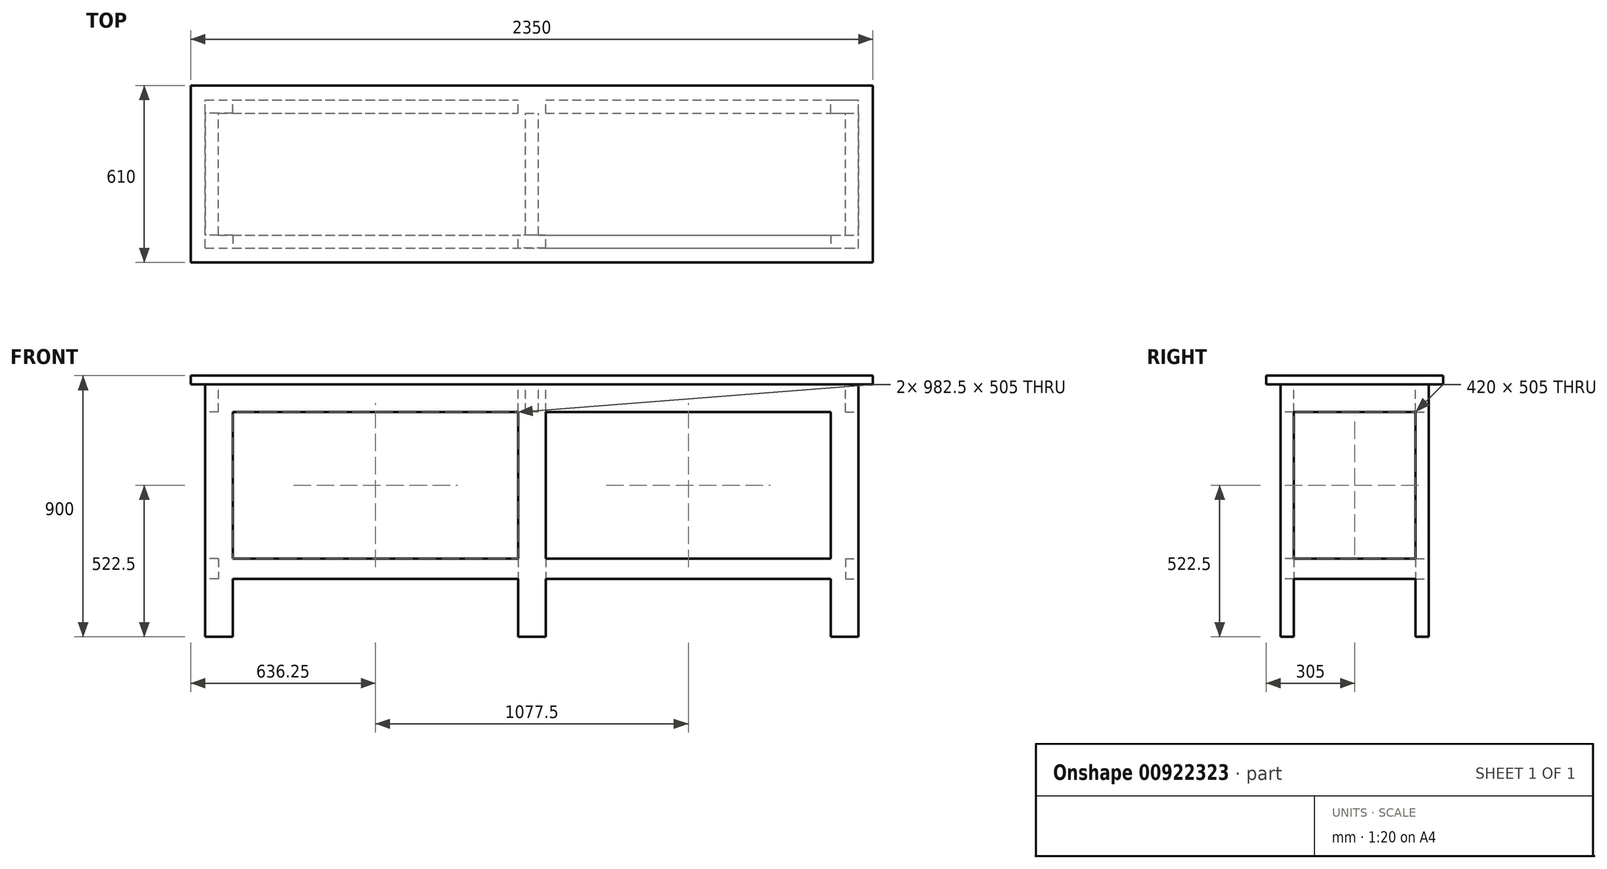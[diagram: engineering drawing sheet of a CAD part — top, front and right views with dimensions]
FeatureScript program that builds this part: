
annotation { "Feature Type Name" : "Feature", "Feature Type Description" : "" }
export const myFeature = defineFeature(function(context is Context, id is Id, definition is map)
    precondition{}
    {
        {
            var Q0;
            Q0=qCreatedBy(makeId("Top.planeOp"),FACE);
            cPlane(context, id + "F0", {"entities" : qUnion([Q0]), "cplaneType" : CPlaneType.OFFSET, "offset" : 900 * mm, "width" : 150 * mm, "height" : 150 * mm});
        }
        {
            var Q0;
            Q0=qCreatedBy(id+"F0.planeOp",FACE);
            var sketch = newSketch(context, id + "F1", { "sketchPlane" : qUnion([Q0])});
            skLineSegment(sketch, "E0.bottom", {"start": v(1175, -305) * mm, "end": v(-1175, -305) * mm});
            skLineSegment(sketch, "E0.top", {"start": v(1175, 305) * mm, "end": v(-1175, 305) * mm});
            skLineSegment(sketch, "E0.left", {"start": v(1175, -305) * mm, "end": v(1175, 305) * mm});
            skLineSegment(sketch, "E0.right", {"start": v(-1175, -305) * mm, "end": v(-1175, 305) * mm});
            skPoint(sketch, "E0.middle", {"position": v(0, 0) * mm});
            skSolve(sketch);
        }
        {
            var Q0;
            Q0=makeQuery(id+"F1.imprint","IMPRINT",FACE,{"disambiguationData":[TD([[makeQuery(id+"F1.imprint","IMPRINT",EDGE,{"derivedFrom":sQuery(id+"F1.wireOp",EDGE,"E0.bottom")}),-1.0]])]});
            extrude(context, id + "F2", {"entities" : qUnion([Q0]), "oppositeDirection" : true, "depth" : 30 * mm, "offsetDistance" : 25 * mm});
        }
        {
            var Q0;
            Q0=makeQuery(id+"F2.opExtrude","CAP_FACE",FACE,{"disambiguationData":[OSD([sQuery(id+"F1.wireOp",EDGE,"E0.bottom"),sQuery(id+"F1.wireOp",EDGE,"E0.top"),sQuery(id+"F1.wireOp",EDGE,"E0.left"),sQuery(id+"F1.wireOp",EDGE,"E0.right")])],"isStart":false});
            var sketch = newSketch(context, id + "F3", { "sketchPlane" : qUnion([Q0])});
            skLineSegment(sketch, "E1.bottom", {"start": v(-1125, 255) * mm, "end": v(-1030, 255) * mm});
            skLineSegment(sketch, "E1.top", {"start": v(-1125, -255) * mm, "end": v(1125, -255) * mm});
            skLineSegment(sketch, "E1.left", {"start": v(-1125, 255) * mm, "end": v(-1125, -255) * mm});
            skLineSegment(sketch, "E1.right", {"start": v(1125, 255) * mm, "end": v(1125, -255) * mm});
            skPoint(sketch, "E1.middle", {"position": v(0, 0) * mm});
            skLineSegment(sketch, "E2.bottom", {"start": v(-1080, 210) * mm, "end": v(-47.5, 210) * mm});
            skLineSegment(sketch, "E2.top", {"start": v(-1080, -210) * mm, "end": v(1080, -210) * mm});
            skLineSegment(sketch, "E2.left", {"start": v(-1080, 210) * mm, "end": v(-1080, -210) * mm});
            skLineSegment(sketch, "E2.right", {"start": v(1080, 210) * mm, "end": v(1080, -210) * mm});
            skLineSegment(sketch, "E3", {"start": v(-1080, 210) * mm, "end": v(-1125, 210) * mm});
            skPoint(sketch, "E4", {"position": v(-1030, 210) * mm});
            skLineSegment(sketch, "E5", {"start": v(-1030, 210) * mm, "end": v(-1030, 255) * mm});
            skLineSegment(sketch, "E6", {"start": v(0, 0) * mm, "end": v(0, 95) * mm, "construction": true});
            skLineSegment(sketch, "E7", {"start": v(0, 0) * mm, "end": v(-86.34, 0) * mm, "construction": true});
            skLineSegment(sketch, "E8.MirrorCS", {"start": v(-1080, -210) * mm, "end": v(-1125, -210) * mm});
            skLineSegment(sketch, "E9.MirrorCS", {"start": v(-1030, -210) * mm, "end": v(-1030, -255) * mm});
            skLineSegment(sketch, "E10.MirrorCS", {"start": v(1030, 210) * mm, "end": v(1030, 255) * mm});
            skLineSegment(sketch, "E11.MirrorCS", {"start": v(1080, 210) * mm, "end": v(1125, 210) * mm});
            skLineSegment(sketch, "E12.MirrorCS", {"start": v(1030, -210) * mm, "end": v(1030, -255) * mm});
            skLineSegment(sketch, "E13.MirrorCS", {"start": v(1080, -210) * mm, "end": v(1125, -210) * mm});
            skLineSegment(sketch, "E14.bottom", {"start": v(22.5, 210) * mm, "end": v(-22.5, 210) * mm});
            skLineSegment(sketch, "E14.top", {"start": v(22.5, -210) * mm, "end": v(-22.5, -210) * mm});
            skLineSegment(sketch, "E14.left", {"start": v(22.5, 210) * mm, "end": v(22.5, -210) * mm});
            skLineSegment(sketch, "E14.right", {"start": v(-22.5, 210) * mm, "end": v(-22.5, -210) * mm});
            skPoint(sketch, "E15.oppositeSnap0", {"position": v(0, 47.5) * mm});
            skLineSegment(sketch, "E15.left", {"start": v(22.5, -47.5) * mm, "end": v(22.5, 47.5) * mm});
            skLineSegment(sketch, "E16", {"start": v(0, -210) * mm, "end": v(0, -255) * mm, "construction": true});
            skLineSegment(sketch, "E17", {"start": v(0, 210) * mm, "end": v(0, 255) * mm, "construction": true});
            skLineSegment(sketch, "E18.bottom", {"start": v(47.5, 255) * mm, "end": v(-47.5, 255) * mm});
            skLineSegment(sketch, "E18.top", {"start": v(47.5, 210) * mm, "end": v(-47.5, 210) * mm});
            skLineSegment(sketch, "E18.left", {"start": v(47.5, 255) * mm, "end": v(47.5, 210) * mm});
            skLineSegment(sketch, "E18.right", {"start": v(-47.5, 255) * mm, "end": v(-47.5, 210) * mm});
            skPoint(sketch, "E18.middle", {"position": v(0, 232.5) * mm});
            skLineSegment(sketch, "E19.bottom", {"start": v(47.5, -210) * mm, "end": v(-47.5, -210) * mm});
            skLineSegment(sketch, "E19.top", {"start": v(47.5, -255) * mm, "end": v(-47.5, -255) * mm});
            skLineSegment(sketch, "E19.left", {"start": v(47.5, -210) * mm, "end": v(47.5, -255) * mm});
            skLineSegment(sketch, "E19.right", {"start": v(-47.5, -210) * mm, "end": v(-47.5, -255) * mm});
            skPoint(sketch, "E19.middle", {"position": v(0, -232.5) * mm});
            skLineSegment(sketch, "E20", {"start": v(-1030, 255) * mm, "end": v(-47.5, 255) * mm});
            skLineSegment(sketch, "E21", {"start": v(-47.5, 255) * mm, "end": v(47.5, 255) * mm});
            skLineSegment(sketch, "E22", {"start": v(47.5, 255) * mm, "end": v(1125, 255) * mm});
            skLineSegment(sketch, "E23", {"start": v(47.5, 210) * mm, "end": v(1080, 210) * mm});
            skLineSegment(sketch, "E24", {"start": v(-47.5, 210) * mm, "end": v(47.5, 210) * mm});
            skSolve(sketch);
        }
        {
            var Q0;
            Q0=makeQuery(id+"F3.imprint","IMPRINT",FACE,{"disambiguationData":[TD([[makeQuery(id+"F3.imprint","IMPRINT",EDGE,{"derivedFrom":sQuery(id+"F3.wireOp",EDGE,"E2.left")}),-1.0]])]});
            var Q1;
            Q1=makeQuery(id+"F3.imprint","IMPRINT",FACE,{"disambiguationData":[TD([[makeQuery(id+"F3.imprint","IMPRINT",EDGE,{"derivedFrom":sQuery(id+"F3.wireOp",EDGE,"E2.right")}),1.0]])]});
            var Q2;
            {var subQ3=sQuery(id+"F3.wireOp",EDGE,"E5");Q2=makeQuery(id+"F3.imprint","IMPRINT",FACE,{"disambiguationData":[TD([[makeQuery(id+"F3.imprint","IMPRINT",EDGE,{"derivedFrom":subQ3}),-1.0]])]});}
            var Q3;
            {var subQ0=sQuery(id+"F3.wireOp",EDGE,"E9.MirrorCS");Q3=makeQuery(id+"F3.imprint","IMPRINT",FACE,{"disambiguationData":[TD([[makeQuery(id+"F3.imprint","IMPRINT",EDGE,{"derivedFrom":subQ0}),1.0]])]});}
            var Q4;
            {var subQ3=sQuery(id+"F3.wireOp",EDGE,"E14.bottom");Q4=makeQuery(id+"F3.imprint","IMPRINT",FACE,{"disambiguationData":[TD([[makeQuery(id+"F3.imprint","IMPRINT",EDGE,{"derivedFrom":subQ3}),1.0]])]});}
            var Q5;
            {var subQ0=sQuery(id+"F3.wireOp",EDGE,"E10.MirrorCS");Q5=makeQuery(id+"F3.imprint","IMPRINT",FACE,{"disambiguationData":[TD([[makeQuery(id+"F3.imprint","IMPRINT",EDGE,{"derivedFrom":subQ0}),1.0]])]});}
            var Q6;
            {var subQ1=sQuery(id+"F3.wireOp",EDGE,"E14.right");Q6=makeQuery(id+"F3.imprint","IMPRINT",FACE,{"disambiguationData":[TD([[makeQuery(id+"F3.imprint","IMPRINT",EDGE,{"derivedFrom":subQ1}),1.0]])]});}
            var Q7;
            {var subQ0=sQuery(id+"F3.wireOp",EDGE,"E12.MirrorCS");Q7=makeQuery(id+"F3.imprint","IMPRINT",FACE,{"disambiguationData":[TD([[makeQuery(id+"F3.imprint","IMPRINT",EDGE,{"derivedFrom":subQ0}),-1.0]])]});}
            extrude(context, id + "F4", {"entities" : qUnion([Q0, Q1, Q2, Q3, Q4, Q5, Q6, Q7]), "operationType" : NewBodyOperationType.ADD, "depth" : 95 * mm, "offsetDistance" : 25 * mm});
        }
        {
            var Q0;
            {var subQ0=sQuery(id+"F3.wireOp",EDGE,"E3");Q0=makeQuery(id+"F3.imprint","IMPRINT",FACE,{"disambiguationData":[TD([[makeQuery(id+"F3.imprint","IMPRINT",EDGE,{"derivedFrom":subQ0}),-1.0]])]});}
            var Q1;
            {var subQ0=sQuery(id+"F3.wireOp",EDGE,"E8.MirrorCS");Q1=makeQuery(id+"F3.imprint","IMPRINT",FACE,{"disambiguationData":[TD([[makeQuery(id+"F3.imprint","IMPRINT",EDGE,{"derivedFrom":subQ0}),1.0]])]});}
            var Q2;
            {var subQ0=sQuery(id+"F3.wireOp",EDGE,"E12.MirrorCS");Q2=makeQuery(id+"F3.imprint","IMPRINT",FACE,{"disambiguationData":[TD([[makeQuery(id+"F3.imprint","IMPRINT",EDGE,{"derivedFrom":subQ0}),1.0]])]});}
            var Q3;
            {var subQ0=sQuery(id+"F3.wireOp",EDGE,"E10.MirrorCS");Q3=makeQuery(id+"F3.imprint","IMPRINT",FACE,{"disambiguationData":[TD([[makeQuery(id+"F3.imprint","IMPRINT",EDGE,{"derivedFrom":subQ0}),-1.0]])]});}
            var Q4;
            Q4=makeQuery(id+"F3.imprint","IMPRINT",FACE,{"disambiguationData":[TD([[makeQuery(id+"F3.imprint","IMPRINT",EDGE,{"derivedFrom":sQuery(id+"F3.wireOp",EDGE,"E15.bottom")}),1.0]])]});
            var Q5;
            Q5=makeQuery(id+"F3.imprint","IMPRINT",FACE,{"disambiguationData":[TD([[makeQuery(id+"F3.imprint","IMPRINT",EDGE,{"derivedFrom":sQuery(id+"F3.wireOp",EDGE,"E18.bottom")}),1.0]])]});
            var Q6;
            Q6=makeQuery(id+"F3.imprint","IMPRINT",FACE,{"disambiguationData":[TD([[makeQuery(id+"F3.imprint","IMPRINT",EDGE,{"derivedFrom":sQuery(id+"F3.wireOp",EDGE,"E19.top")}),-1.0]])]});
            var Q7;
            {var subQ3=sQuery(id+"F3.wireOp",EDGE,"E18.left");Q7=makeQuery(id+"F3.imprint","IMPRINT",FACE,{"disambiguationData":[TD([[makeQuery(id+"F3.imprint","IMPRINT",EDGE,{"derivedFrom":subQ3}),-1.0]])]});}
            extrude(context, id + "F5", {"entities" : qUnion([Q0, Q1, Q2, Q3, Q4, Q5, Q6, Q7]), "operationType" : NewBodyOperationType.ADD, "depth" : (900 - 30) * mm, "offsetDistance" : 25 * mm});
        }
        {
            var Q0;
            Q0=qCreatedBy(makeId("Top.planeOp"),FACE);
            cPlane(context, id + "F6", {"entities" : qUnion([Q0]), "cplaneType" : CPlaneType.OFFSET, "offset" : 200 * mm, "width" : 150 * mm, "height" : 150 * mm});
        }
        {
            var Q0;
            Q0=qCreatedBy(id+"F6.planeOp",FACE);
            var sketch = newSketch(context, id + "F7", { "sketchPlane" : qUnion([Q0])});
            skLineSegment(sketch, "E25.bottom", {"start": v(-1030, 255) * mm, "end": v(1030, 255) * mm});
            skLineSegment(sketch, "E25.top", {"start": v(-1030, -255) * mm, "end": v(1030, -255) * mm});
            skLineSegment(sketch, "E25.left", {"start": v(-1125, 210) * mm, "end": v(-1125, -210) * mm});
            skLineSegment(sketch, "E25.right", {"start": v(1125, 210) * mm, "end": v(1125, -210) * mm});
            skPoint(sketch, "E25.middle", {"position": v(0, 0) * mm});
            skLineSegment(sketch, "E26.bottom", {"start": v(-1030, 210) * mm, "end": v(1030, 210) * mm});
            skLineSegment(sketch, "E26.top", {"start": v(-1030, -210) * mm, "end": v(1030, -210) * mm});
            skLineSegment(sketch, "E26.left", {"start": v(-1080, 210) * mm, "end": v(-1080, -210) * mm});
            skLineSegment(sketch, "E26.right", {"start": v(1080, 210) * mm, "end": v(1080, -210) * mm});
            skLineSegment(sketch, "E27", {"start": v(-1080, 210) * mm, "end": v(-1125, 210) * mm});
            skPoint(sketch, "E28", {"position": v(-1030, 210) * mm});
            skLineSegment(sketch, "E29", {"start": v(-1030, 210) * mm, "end": v(-1030, 255) * mm});
            skLineSegment(sketch, "E30.MirrorCS", {"start": v(-1080, -210) * mm, "end": v(-1125, -210) * mm});
            skLineSegment(sketch, "E31.MirrorCS", {"start": v(-1030, -210) * mm, "end": v(-1030, -255) * mm});
            skLineSegment(sketch, "E32.MirrorCS", {"start": v(1030, 210) * mm, "end": v(1030, 255) * mm});
            skLineSegment(sketch, "E33.MirrorCS", {"start": v(1080, 210) * mm, "end": v(1125, 210) * mm});
            skLineSegment(sketch, "E34.MirrorCS", {"start": v(1030, -210) * mm, "end": v(1030, -255) * mm});
            skLineSegment(sketch, "E35.MirrorCS", {"start": v(1080, -210) * mm, "end": v(1125, -210) * mm});
            skLineSegment(sketch, "E36.bottom", {"start": v(22.5, 210) * mm, "end": v(-22.5, 210) * mm});
            skLineSegment(sketch, "E36.top", {"start": v(22.5, -210) * mm, "end": v(-22.5, -210) * mm});
            skLineSegment(sketch, "E36.left", {"start": v(22.5, 210) * mm, "end": v(22.5, -210) * mm});
            skLineSegment(sketch, "E36.right", {"start": v(-22.5, 210) * mm, "end": v(-22.5, -210) * mm});
            skPoint(sketch, "E37.oppositeSnap0", {"position": v(0, 47.5) * mm});
            skLineSegment(sketch, "E37.left", {"start": v(22.5, -47.5) * mm, "end": v(22.5, 47.5) * mm});
            skPoint(sketch, "E38.orphan", {"position": v(-1125, 255) * mm});
            skPoint(sketch, "E39.orphan", {"position": v(-1125, -255) * mm});
            skPoint(sketch, "E40.orphan", {"position": v(1125, -255) * mm});
            skPoint(sketch, "E41.orphan", {"position": v(1125, 255) * mm});
            skLineSegment(sketch, "E42", {"start": v(0, 210) * mm, "end": v(0, 255) * mm, "construction": true});
            skLineSegment(sketch, "E43.bottom", {"start": v(22.5, 210) * mm, "end": v(67.5, 210) * mm});
            skLineSegment(sketch, "E43.top", {"start": v(22.5, 255) * mm, "end": v(67.5, 255) * mm});
            skLineSegment(sketch, "E44.bottom", {"start": v(22.5, -210) * mm, "end": v(67.5, -210) * mm});
            skLineSegment(sketch, "E44.top", {"start": v(22.5, -255) * mm, "end": v(47.5, -255) * mm});
            skLineSegment(sketch, "E45", {"start": v(0, -210) * mm, "end": v(0, -255) * mm, "construction": true});
            skLineSegment(sketch, "E46.bottom", {"start": v(47.5, -255) * mm, "end": v(-47.5, -255) * mm, "construction": true});
            skLineSegment(sketch, "E46.top", {"start": v(47.5, -210) * mm, "end": v(-47.5, -210) * mm, "construction": true});
            skLineSegment(sketch, "E46.left", {"start": v(47.5, -255) * mm, "end": v(47.5, -210) * mm});
            skLineSegment(sketch, "E46.right", {"start": v(-47.5, -255) * mm, "end": v(-47.5, -210) * mm});
            skPoint(sketch, "E46.middle", {"position": v(0, -232.5) * mm});
            skLineSegment(sketch, "E47.bottom", {"start": v(47.5, 255) * mm, "end": v(-47.5, 255) * mm, "construction": true});
            skLineSegment(sketch, "E47.top", {"start": v(47.5, 210) * mm, "end": v(-47.5, 210) * mm, "construction": true});
            skLineSegment(sketch, "E47.left", {"start": v(47.5, 255) * mm, "end": v(47.5, 210) * mm});
            skLineSegment(sketch, "E47.right", {"start": v(-47.5, 255) * mm, "end": v(-47.5, 210) * mm});
            skPoint(sketch, "E47.middle", {"position": v(0, 232.5) * mm});
            skSolve(sketch);
        }
        {
            var Q0;
            Q0=makeQuery(id+"F7.imprint","IMPRINT",FACE,{"disambiguationData":[TD([[makeQuery(id+"F7.imprint","IMPRINT",EDGE,{"derivedFrom":sQuery(id+"F7.wireOp",EDGE,"E25.left")}),1.0]])]});
            var Q1;
            Q1=makeQuery(id+"F7.imprint","IMPRINT",FACE,{"disambiguationData":[TD([[makeQuery(id+"F7.imprint","IMPRINT",EDGE,{"derivedFrom":sQuery(id+"F7.wireOp",EDGE,"E25.top")}),1.0]])]});
            var Q2;
            Q2=makeQuery(id+"F7.imprint","IMPRINT",FACE,{"disambiguationData":[TD([[makeQuery(id+"F7.imprint","IMPRINT",EDGE,{"derivedFrom":sQuery(id+"F7.wireOp",EDGE,"E25.bottom")}),-1.0]])]});
            var Q3;
            Q3=makeQuery(id+"F7.imprint","IMPRINT",FACE,{"disambiguationData":[TD([[makeQuery(id+"F7.imprint","IMPRINT",EDGE,{"derivedFrom":sQuery(id+"F7.wireOp",EDGE,"E25.right")}),-1.0]])]});
            var Q4;
            {var subQ3=sQuery(id+"F7.wireOp",EDGE,"E36.bottom");Q4=makeQuery(id+"F7.imprint","IMPRINT",FACE,{"disambiguationData":[TD([[makeQuery(id+"F7.imprint","IMPRINT",EDGE,{"derivedFrom":subQ3}),1.0]])]});}
            var Q5;
            {var subQ0=sQuery(id+"F7.wireOp",EDGE,"E29");Q5=makeQuery(id+"F7.imprint","IMPRINT",FACE,{"disambiguationData":[TD([[makeQuery(id+"F7.imprint","IMPRINT",EDGE,{"derivedFrom":subQ0}),-1.0]])]});}
            var Q6;
            {var subQ1=sQuery(id+"F7.wireOp",EDGE,"E31.MirrorCS");Q6=makeQuery(id+"F7.imprint","IMPRINT",FACE,{"disambiguationData":[TD([[makeQuery(id+"F7.imprint","IMPRINT",EDGE,{"derivedFrom":subQ1}),1.0]])]});}
            var Q7;
            {var subQ0=sQuery(id+"F7.wireOp",EDGE,"E34.MirrorCS");Q7=makeQuery(id+"F7.imprint","IMPRINT",FACE,{"disambiguationData":[TD([[makeQuery(id+"F7.imprint","IMPRINT",EDGE,{"derivedFrom":subQ0}),-1.0]])]});}
            var Q8;
            {var subQ4=sQuery(id+"F7.wireOp",EDGE,"E32.MirrorCS");Q8=makeQuery(id+"F7.imprint","IMPRINT",FACE,{"disambiguationData":[TD([[makeQuery(id+"F7.imprint","IMPRINT",EDGE,{"derivedFrom":subQ4}),1.0]])]});}
            extrude(context, id + "F8", {"entities" : qUnion([Q0, Q1, Q2, Q3, Q4, Q5, Q6, Q7, Q8]), "operationType" : NewBodyOperationType.ADD, "depth" : 70 * mm, "offsetDistance" : 25 * mm});
        }
    });
